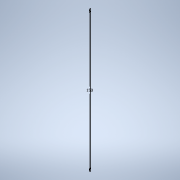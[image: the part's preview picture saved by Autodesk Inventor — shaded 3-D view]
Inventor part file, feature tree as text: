
AUTODESK INVENTOR PART (.ipt)
format: ipt  version: 2020 (Build 240168000, 168)  size: 82,944 bytes
history: native  units: in
note: dims shown in document units (in); Inventor stores cm internally (conversion verified against a paired STEP export)
features: sketch x1
ambient origin geometry x8: Origin, YZ Plane, XZ Plane, XY Plane, X Axis, Y Axis, Z Axis, Center Point
feature tree (1):
  sketch  "Sketch1"  dims[d0=5.9055in]
